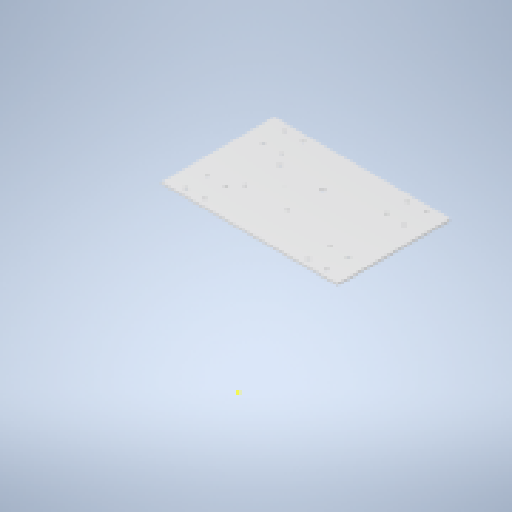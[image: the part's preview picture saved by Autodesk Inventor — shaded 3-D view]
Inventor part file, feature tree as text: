
AUTODESK INVENTOR PART (.ipt)
format: ipt  version: 2023.2 (Build 272271000, 271)  size: 191,488 bytes
history: native  units: in
note: dims shown in document units (in); Inventor stores cm internally (conversion verified against a paired STEP export)
features: extrude x3, sketch x2
ambient origin geometry x8: Origin, YZ Plane, XZ Plane, XY Plane, X Axis, Y Axis, Z Axis, Center Point
bodies: Solid1 (feature_tree)
feature tree (5):
  sketch  "Sketch1"  dims[d2=0.5394in d4=2.3819in]
  extrude  "Extrusion1"  Depth=2.3819in
  sketch  "Sketch2"  dims[d5=0.2008in d6=0.2008in d7=0.2008in d8=0.2795in d9=0.1181in d10=0.0in d11=0.0787in d12=0.1181in d13=0.0in d15=1.9685in d17=3.937in d18=0.9843in d19=0.6004in d20=0.2008in d21=0.5118in d22=3.5433in d23=6.2992in d24=4.3307in d25=0.0in d26=0.0in d27=12.5984in]
  extrude  "Extrusion2"  Depth=12.5984in
  extrude  "Extrusion3"  Depth=12.5984in
